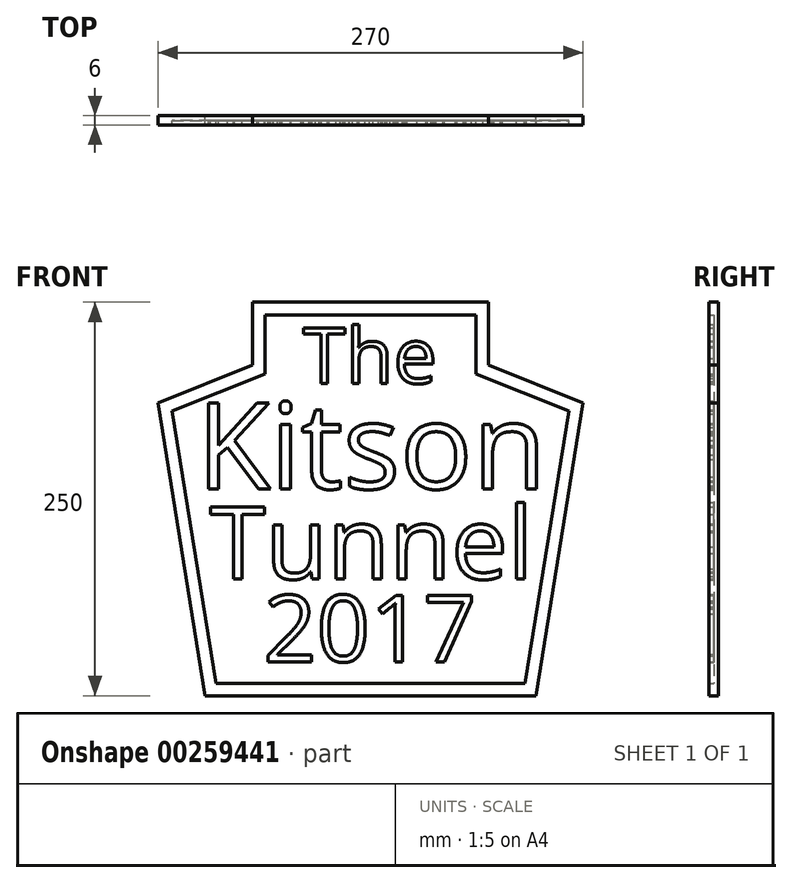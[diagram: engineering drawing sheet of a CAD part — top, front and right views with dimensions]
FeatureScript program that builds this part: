
annotation { "Feature Type Name" : "Feature", "Feature Type Description" : "" }
export const myFeature = defineFeature(function(context is Context, id is Id, definition is map)
    precondition{}
    {
        {
            var Q0;
            Q0=qCreatedBy(makeId("Front.planeOp"),FACE);
            var sketch = newSketch(context, id + "F0", { "sketchPlane" : qUnion([Q0])});
            skLineSegment(sketch, "E0", {"start": v(0, 0) * mm, "end": v(210, 0) * mm});
            skLineSegment(sketch, "E1", {"start": v(105, 0) * mm, "end": v(105, 250) * mm, "construction": true});
            skLineSegment(sketch, "E2", {"start": v(105, 250) * mm, "end": v(30, 250) * mm});
            skLineSegment(sketch, "E3", {"start": v(30, 250) * mm, "end": v(30, 210) * mm});
            skLineSegment(sketch, "E4", {"start": v(30, 210) * mm, "end": v(-30, 186.13) * mm});
            skLineSegment(sketch, "E5", {"start": v(-30, 186.13) * mm, "end": v(0, 0) * mm});
            skLineSegment(sketch, "E6.MirrorCS", {"start": v(105, 250) * mm, "end": v(180, 250) * mm});
            skLineSegment(sketch, "E7.MirrorCS", {"start": v(180, 250) * mm, "end": v(180, 210) * mm});
            skLineSegment(sketch, "E8.MirrorCS", {"start": v(180, 210) * mm, "end": v(240, 186.13) * mm});
            skLineSegment(sketch, "E9.MirrorCS", {"start": v(240, 186.13) * mm, "end": v(210, 0) * mm});
            skLineSegment(sketch, "E10", {"start": v(-30, 186.13) * mm, "end": v(105, 186.13) * mm, "construction": true});
            skSolve(sketch);
        }
        {
            var Q0;
            Q0 = qSketchRegion(id + "F0", true);
            extrude(context, id + "F1", {"entities" : qUnion([Q0]), "depth" : 3 * mm});
        }
        {
            var Q0;
            Q0=makeQuery(id+"F1.opExtrude","CAP_FACE",FACE,{"disambiguationData":[OSD([sQuery(id+"F0.wireOp",EDGE,"E0"),sQuery(id+"F0.wireOp",EDGE,"E2"),sQuery(id+"F0.wireOp",EDGE,"E3"),sQuery(id+"F0.wireOp",EDGE,"E4"),sQuery(id+"F0.wireOp",EDGE,"E5"),sQuery(id+"F0.wireOp",EDGE,"E6.MirrorCS"),sQuery(id+"F0.wireOp",EDGE,"E7.MirrorCS"),sQuery(id+"F0.wireOp",EDGE,"E8.MirrorCS"),sQuery(id+"F0.wireOp",EDGE,"E9.MirrorCS")])],"isStart":false});
            var sketch = newSketch(context, id + "F2", { "sketchPlane" : qUnion([Q0])});
            skLineSegment(sketch, "E11.1", {"start": v(15, 266.6) * mm, "end": v(-15.3, 203.26) * mm, "construction": true});
            skLineSegment(sketch, "E11.3", {"start": v(-15.3, 203.26) * mm, "end": v(12.92, 15) * mm, "construction": true});
            skLineSegment(sketch, "E11.5", {"start": v(135, 266.6) * mm, "end": v(165.3, 203.26) * mm, "construction": true});
            skLineSegment(sketch, "E11.6", {"start": v(165.3, 203.26) * mm, "end": v(137.08, 15) * mm, "construction": true});
            skLineSegment(sketch, "E11.7", {"start": v(12.92, 15) * mm, "end": v(137.08, 15) * mm, "construction": true});
            skLineSegment(sketch, "E12", {"start": v(105, 250) * mm, "end": v(105, 0) * mm, "construction": true});
            skText(sketch, "E13", { "text": "Kitson", "fontName": "OpenSans-Regular.ttf"});
            skPoint(sketch, "E14", {"position": v(302.06, 145.94) * mm});
            skText(sketch, "E15", { "text": "Tunnel", "fontName": "OpenSans-Regular.ttf"});
            skText(sketch, "E16", { "text": "2017", "fontName": "OpenSans-Regular.ttf"});
            skText(sketch, "E17", { "text": "The", "fontName": "OpenSans-Regular.ttf"});
            const initialGuessF2  = {"E13": [-0.00535, 0.13153, 1, 0, 0.05481], "E15": [0.0029, 0.07422, 1, 0, 0.04613], "E16": [0.03702, 0.02165, 1, 0, 0.04255], "E17": [0.06218, 0.19845, 1, 0, 0.03542]};
            skSetInitialGuess(sketch, initialGuessF2);
            skSolve(sketch);
        }
        {
            var Q0;
            Q0 = qSketchRegion(id + "F2", true);
            extrude(context, id + "F3", {"entities" : qUnion([Q0]), "operationType" : NewBodyOperationType.ADD, "depth" : 3 * mm});
        }
        {
            var Q0;
            {var subQ0=sQuery(id+"F0.wireOp",EDGE,"E3");var subQ1=sQuery(id+"F0.wireOp",EDGE,"E9.MirrorCS");var subQ2=sQuery(id+"F0.wireOp",EDGE,"E8.MirrorCS");var subQ3=sQuery(id+"F0.wireOp",EDGE,"E7.MirrorCS");var subQ4=sQuery(id+"F0.wireOp",EDGE,"E5");var subQ5=sQuery(id+"F0.wireOp",EDGE,"E0");var subQ6=sQuery(id+"F0.wireOp",EDGE,"E4");var subQ7=sQuery(id+"F0.wireOp",EDGE,"E6.MirrorCS");var subQ8=sQuery(id+"F0.wireOp",EDGE,"E2");Q0=makeQuery(id+"F3.boolean.opBoolean","SPLIT",FACE,{"disambiguationData":[TD([makeQuery(id+"F1.opExtrude","SWEPT_FACE",FACE,{"disambiguationData":[OSD([subQ5])]})])],"derivedFrom":makeQuery(id+"F1.opExtrude","CAP_FACE",FACE,{"disambiguationData":[OSD([subQ5,subQ8,subQ0,subQ6,subQ4,subQ7,subQ3,subQ2,subQ1])],"isStart":false})});}
            var sketch = newSketch(context, id + "F4", { "sketchPlane" : qUnion([Q0])});
            skLineSegment(sketch, "E18.0", {"start": v(38, 242) * mm, "end": v(172, 242) * mm});
            skLineSegment(sketch, "E18.1", {"start": v(172, 242) * mm, "end": v(172, 204.57) * mm});
            skLineSegment(sketch, "E18.2", {"start": v(38, 242) * mm, "end": v(38, 204.57) * mm});
            skLineSegment(sketch, "E18.3", {"start": v(172, 204.57) * mm, "end": v(231.08, 181.07) * mm});
            skLineSegment(sketch, "E18.4", {"start": v(38, 204.57) * mm, "end": v(-21.08, 181.07) * mm});
            skLineSegment(sketch, "E18.5", {"start": v(-21.08, 181.07) * mm, "end": v(6.81, 8) * mm});
            skLineSegment(sketch, "E18.6", {"start": v(6.81, 8) * mm, "end": v(203.19, 8) * mm});
            skLineSegment(sketch, "E18.7", {"start": v(231.08, 181.07) * mm, "end": v(203.19, 8) * mm});
            skLineSegment(sketch, "E19.0", {"start": v(30, 250) * mm, "end": v(30, 210) * mm});
            skLineSegment(sketch, "E19.1", {"start": v(30, 210) * mm, "end": v(-30, 186.13) * mm});
            skLineSegment(sketch, "E19.2", {"start": v(30, 250) * mm, "end": v(180, 250) * mm});
            skLineSegment(sketch, "E19.3", {"start": v(-30, 186.13) * mm, "end": v(0, 0) * mm});
            skLineSegment(sketch, "E19.4", {"start": v(180, 250) * mm, "end": v(180, 210) * mm});
            skLineSegment(sketch, "E19.5", {"start": v(180, 210) * mm, "end": v(240, 186.13) * mm});
            skLineSegment(sketch, "E19.6", {"start": v(240, 186.13) * mm, "end": v(210, 0) * mm});
            skLineSegment(sketch, "E19.7", {"start": v(0, 0) * mm, "end": v(210, 0) * mm});
            skSolve(sketch);
        }
        {
            var Q0;
            Q0 = qSketchRegion(id + "F4", true);
            extrude(context, id + "F5", {"entities" : qUnion([Q0]), "operationType" : NewBodyOperationType.ADD, "depth" : 3 * mm});
        }
    });
